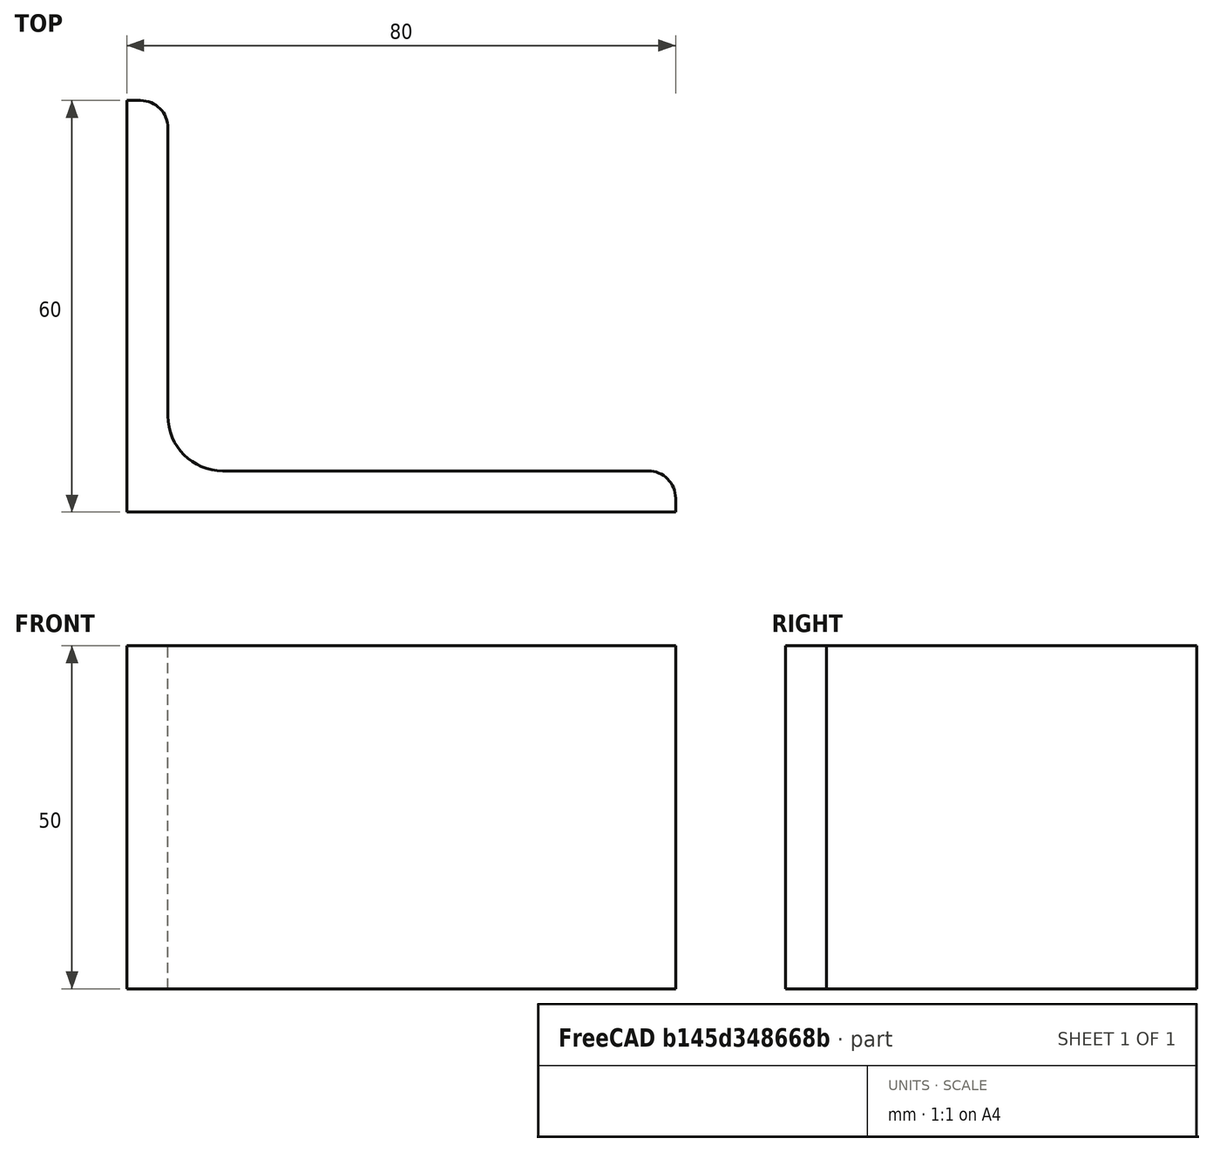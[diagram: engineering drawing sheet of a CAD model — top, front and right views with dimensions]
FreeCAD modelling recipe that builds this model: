
FCSTD DOCUMENT  (FreeCAD 0.15R4671 (Git))
Label: Angle Bar 80x60x6 EN10056 S235JR
License: All rights reserved
LicenseURL: http://en.wikipedia.org/wiki/All_rights_reserved
objects: Sketcher::SketchObject×1, Part::Extrusion×1
note: 2 computed .brp shape members not serialized (recipe doc carries the construction recipe); baked Part::Feature solids carry a one-line shape summary decoded from their .brp

FEATURE [Sketcher::SketchObject] Sketch
  sketch-geometry (9):
    g0: LineSegment StartX=0 StartY=0 StartZ=0 EndX=80 EndY=0 EndZ=0
    g1: LineSegment StartX=80 StartY=0 StartZ=0 EndX=80 EndY=2 EndZ=0
    g2: LineSegment StartX=76 StartY=6 StartZ=0 EndX=14 EndY=6 EndZ=0
    g3: LineSegment StartX=0 StartY=0 StartZ=0 EndX=0 EndY=60 EndZ=0
    g4: LineSegment StartX=0 StartY=60 StartZ=0 EndX=2 EndY=60 EndZ=0
    g5: LineSegment StartX=6 StartY=56 StartZ=0 EndX=6 EndY=14 EndZ=0
    g6: ArcOfCircle CenterX=14 CenterY=14 CenterZ=0 NormalX=0 NormalY=0 NormalZ=1 Radius=8 StartAngle=3.14159 EndAngle=4.71239
    g7: ArcOfCircle CenterX=2 CenterY=56 CenterZ=0 NormalX=0 NormalY=0 NormalZ=1 Radius=4 StartAngle=0 EndAngle=1.5708
    g8: ArcOfCircle CenterX=76 CenterY=2 CenterZ=0 NormalX=0 NormalY=0 NormalZ=1 Radius=4 StartAngle=0 EndAngle=1.5708
  constraints (23):
    c: Coincident(g0,g-1)
    c: Horizontal(g0)
    c: Coincident(g1,g0)
    c: Vertical(g1)
    c: Horizontal(g2)
    c: Coincident(g3,g-1)
    c: Vertical(g3)
    c: Coincident(g4,g3)
    c: Horizontal(g4)
    c: Vertical(g5)
    c: Tangent(g5,g6) = -1.5708
    c: Tangent(g2,g6) = 1.5708
    c: Tangent(g4,g7) = 1.5708
    c: Tangent(g5,g7) = 1.5708
    c: Tangent(g2,g8) = -1.5708
    c: Tangent(g1,g8) = -1.5708
    c: DistanceX(g0) = 80
    c: DistanceY(g3) = 60
    c: DistanceY(g0,g2) = 6
    c: DistanceX(g3,g5) = 6
    c: Radius(g6) = 8
    c: Radius(g8) = 4
    c: Radius(g7) = 4
FEATURE [Part::Extrusion] Extrude  label="Angle Bar 80x60x6 EN10056 S235JR"
  Base = -> Sketch
  Dir = (0,0,50)
  Solid = true
